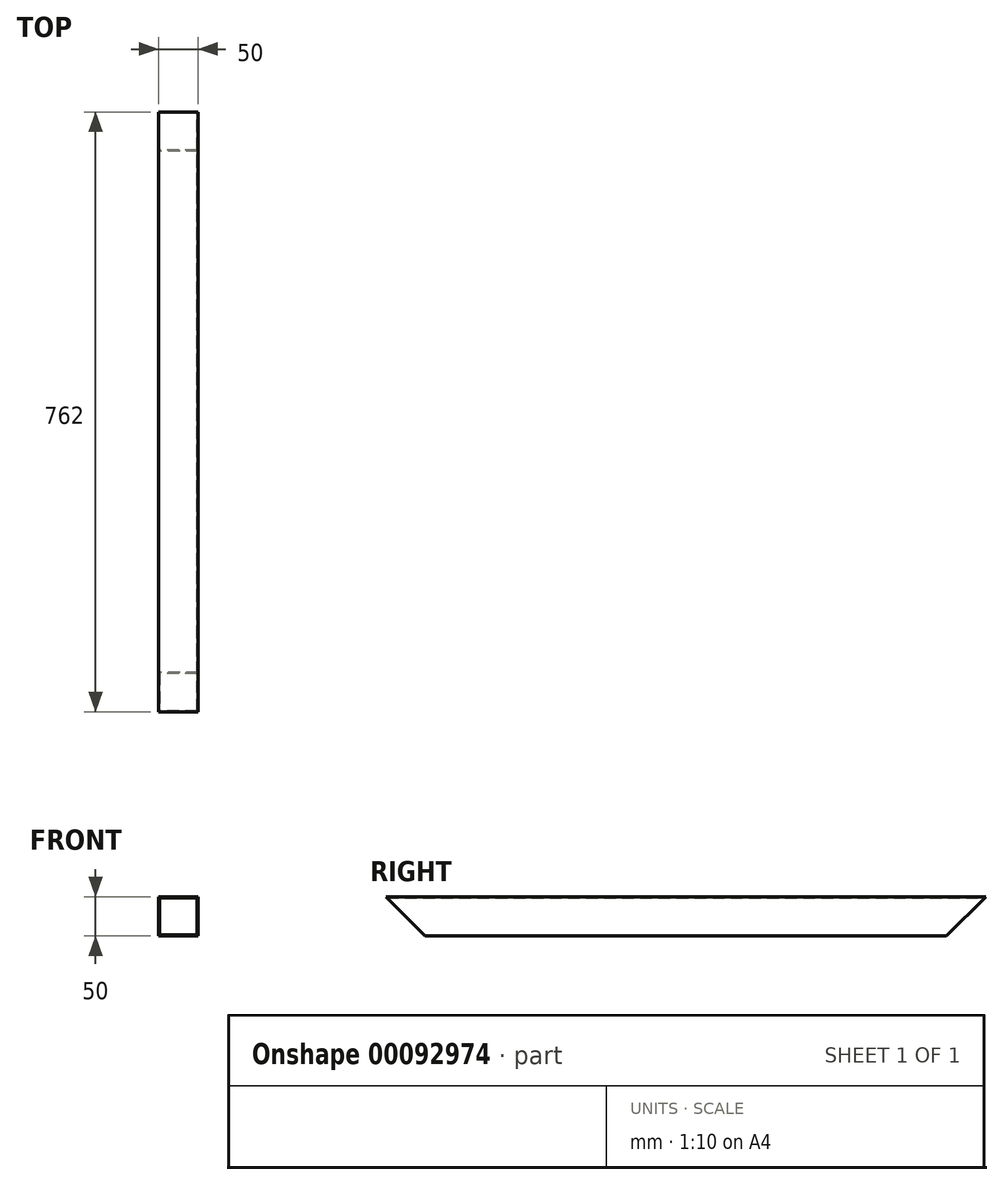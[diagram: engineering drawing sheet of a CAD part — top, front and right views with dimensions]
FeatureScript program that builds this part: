
annotation { "Feature Type Name" : "Feature", "Feature Type Description" : "" }
export const myFeature = defineFeature(function(context is Context, id is Id, definition is map)
    precondition{}
    {
        {
            var Q0;
            Q0=qCreatedBy(makeId("Front.planeOp"),FACE);
            var sketch = newSketch(context, id + "F0", { "sketchPlane" : qUnion([Q0])});
            skLineSegment(sketch, "E0.bottom", {"start": v(-25, 25) * mm, "end": v(25, 25) * mm});
            skLineSegment(sketch, "E0.top", {"start": v(-25, -25) * mm, "end": v(25, -25) * mm});
            skLineSegment(sketch, "E0.left", {"start": v(-25, 25) * mm, "end": v(-25, -25) * mm});
            skLineSegment(sketch, "E0.right", {"start": v(25, 25) * mm, "end": v(25, -25) * mm});
            skPoint(sketch, "E0.middle", {"position": v(0, 0) * mm});
            skLineSegment(sketch, "E1.bottom", {"start": v(-23.75, 23.75) * mm, "end": v(23.75, 23.75) * mm});
            skLineSegment(sketch, "E1.top", {"start": v(-23.75, -23.75) * mm, "end": v(23.75, -23.75) * mm});
            skLineSegment(sketch, "E1.left", {"start": v(-23.75, 23.75) * mm, "end": v(-23.75, -23.75) * mm});
            skLineSegment(sketch, "E1.right", {"start": v(23.75, 23.75) * mm, "end": v(23.75, -23.75) * mm});
            skSolve(sketch);
        }
        {
            var Q0;
            Q0 = qSketchRegion(id + "F0", true);
            extrude(context, id + "F1", {"entities" : qUnion([Q0]), "endBound" : BoundingType.SYMMETRIC, "depth" : 762 * mm});
        }
        {
            var Q0;
            Q0=qCreatedBy(makeId("Right.planeOp"),FACE);
            var sketch = newSketch(context, id + "F2", { "sketchPlane" : qUnion([Q0])});
            skLineSegment(sketch, "E2.0", {"start": v(-381, 25) * mm, "end": v(-381, -25) * mm});
            skLineSegment(sketch, "E3.0", {"start": v(-381, -25) * mm, "end": v(-331, -25) * mm});
            skLineSegment(sketch, "E4.0", {"start": v(381, 25) * mm, "end": v(381, -25) * mm});
            skLineSegment(sketch, "E5", {"start": v(-381, 25) * mm, "end": v(-331, -25) * mm});
            skLineSegment(sketch, "E6", {"start": v(381, 25) * mm, "end": v(331, -25) * mm});
            skLineSegment(sketch, "E7.trimOffspring", {"start": v(331, -25) * mm, "end": v(381, -25) * mm});
            skSolve(sketch);
        }
        {
            var Q0;
            Q0=makeQuery(id+"F2.imprint","IMPRINT",FACE,{"disambiguationData":[TD([[makeQuery(id+"F2.imprint","IMPRINT",EDGE,{"derivedFrom":sQuery(id+"F2.wireOp",EDGE,"E4.0")}),-1.0]])]});
            var Q1;
            Q1=makeQuery(id+"F2.imprint","IMPRINT",FACE,{"disambiguationData":[TD([[makeQuery(id+"F2.imprint","IMPRINT",EDGE,{"derivedFrom":sQuery(id+"F2.wireOp",EDGE,"E2.0")}),1.0]])]});
            extrude(context, id + "F3", {"entities" : qUnion([Q0, Q1]), "operationType" : NewBodyOperationType.REMOVE, "endBound" : BoundingType.SYMMETRIC, "depth" : 60 * mm});
        }
    });
